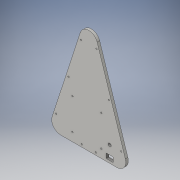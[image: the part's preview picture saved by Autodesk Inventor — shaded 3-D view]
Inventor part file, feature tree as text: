
AUTODESK INVENTOR PART (.ipt)
format: ipt  version: 2016 (Build 200138000, 138)  size: 179,712 bytes
history: native  units: in
note: dims shown in document units (in); Inventor stores cm internally (conversion verified against a paired STEP export)
features: fillet x4, sketch x3, extrude x3, plane x1
ambient origin geometry x8: Origin, YZ Plane, XZ Plane, XY Plane, X Axis, Y Axis, Z Axis, Center Point
bodies: Body1 (feature_tree)
feature tree (11):
  sketch  "Sketch1"  dims[d39=1.25in d40=1.25in d41=1.0in d42=1.0in d43=1.0in d44=0.4in d45=0.4in d46=0.05in d47=0.05in d48=0.4in d49=0.4in d50=0.1in d51=0.1in d52=0.1in d53=0.1in d71=2.2in]
  plane  "Work Plane1"
  sketch  "Sketch2"  dims[d73=2.05in d74=0.1in d75=0.1in d76=0.1in]
  extrude  "Extrusion8"  Depth=0.05in
  extrude  "Extrusion10"  Depth=0.1in
  fillet  "Fillet1"  Radius=0.1in
  fillet  "Fillet2"  Radius=0.1in
  extrude  "Extrusion11"  Depth=0.025in
  fillet  "Fillet5"  Radius=0.6in
  fillet  "Fillet6"  Radius=1.15in
  sketch  "Sketch3"  dims[d77=0.1in d80=2.05in d81=0.6in d82=1.15in d91=0.5in d92=0.5in d93=0.18in d94=0.0in d97=0.09in d98=0.5in d99=0.25in d100=1.0in d101=0.0in d102=0.025in d103=0.025in d106=0.22in d107=1.0in d108=0.0in d109=1.4834in d110=0.025in d111=0.025in]
